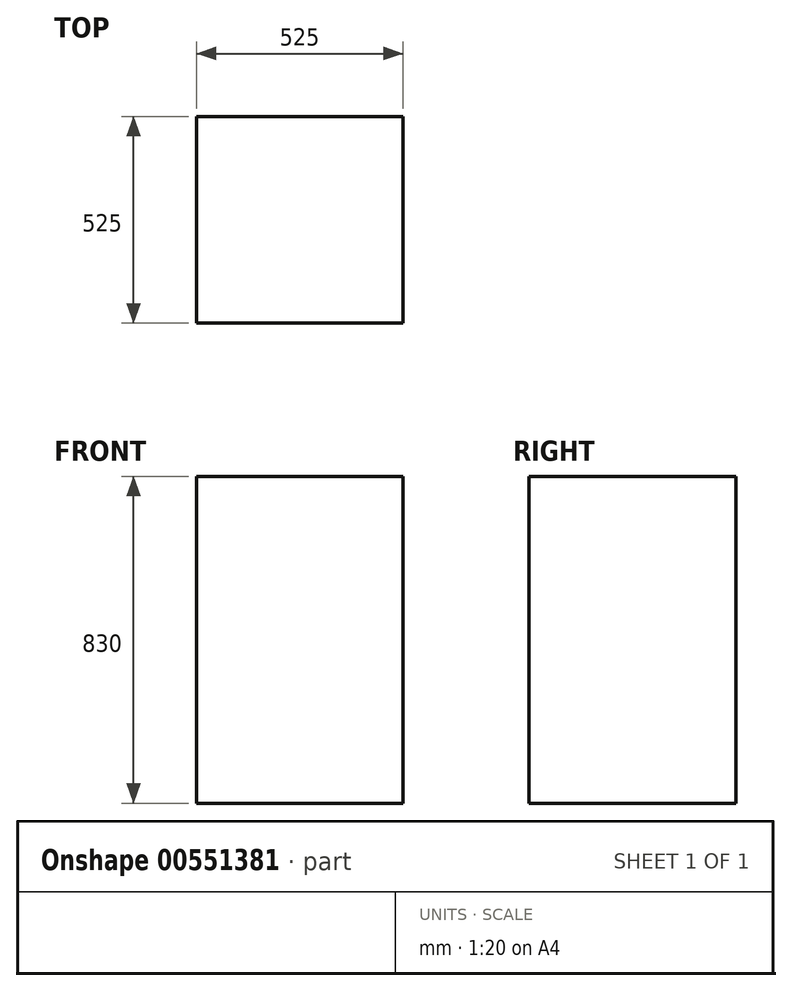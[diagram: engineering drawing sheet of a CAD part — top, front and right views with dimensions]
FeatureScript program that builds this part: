
annotation { "Feature Type Name" : "Feature", "Feature Type Description" : "" }
export const myFeature = defineFeature(function(context is Context, id is Id, definition is map)
    precondition{}
    {
        {
            var Q0;
            Q0=qCreatedBy(makeId("Top.planeOp"),FACE);
            var sketch = newSketch(context, id + "F0", { "sketchPlane" : qUnion([Q0])});
            skLineSegment(sketch, "E0.bottom", {"start": v(262.5, -262.5) * mm, "end": v(-262.5, -262.5) * mm});
            skLineSegment(sketch, "E0.top", {"start": v(262.5, 262.5) * mm, "end": v(-262.5, 262.5) * mm});
            skLineSegment(sketch, "E0.left", {"start": v(262.5, -262.5) * mm, "end": v(262.5, 262.5) * mm});
            skLineSegment(sketch, "E0.right", {"start": v(-262.5, -262.5) * mm, "end": v(-262.5, 262.5) * mm});
            skPoint(sketch, "E0.middle", {"position": v(0, 0) * mm});
            skSolve(sketch);
        }
        {
            var Q0;
            Q0=makeQuery(id+"F0.imprint","IMPRINT",FACE,{"disambiguationData":[TD([[makeQuery(id+"F0.imprint","IMPRINT",EDGE,{"derivedFrom":sQuery(id+"F0.wireOp",EDGE,"E0.bottom")}),-1.0]])]});
            extrude(context, id + "F1", {"entities" : qUnion([Q0]), "depth" : 830 * mm, "offsetDistance" : 25 * mm});
        }
    });
